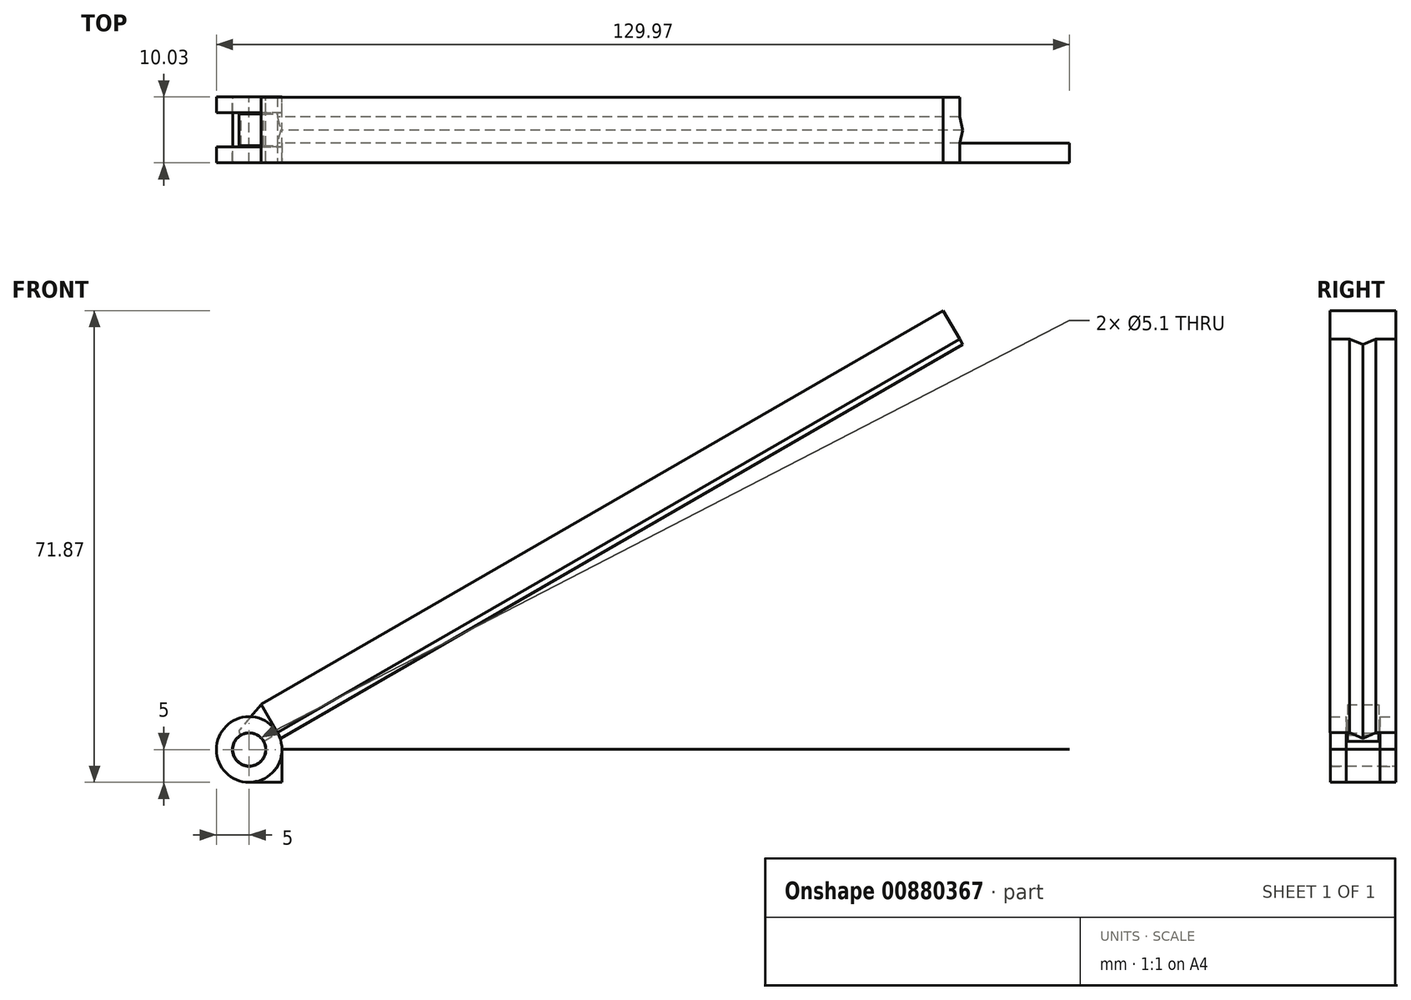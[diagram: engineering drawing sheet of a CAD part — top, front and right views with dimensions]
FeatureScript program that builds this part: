
annotation { "Feature Type Name" : "Feature", "Feature Type Description" : "" }
export const myFeature = defineFeature(function(context is Context, id is Id, definition is map)
    precondition{}
    {
        {
            assignVariable(context, id + "F0", {"name" : "len", "anyValue" : 1.33});
        }
        {
            var Q0;
            Q0=qCreatedBy(makeId("Front.planeOp"),FACE);
            var sketch = newSketch(context, id + "F1", { "sketchPlane" : qUnion([Q0])});
            skPoint(sketch, "E0.middle", {"position": v(0, 0) * mm});
            skLineSegment(sketch, "E1", {"start": v(0, -47.5) * mm, "end": v(0, -45) * mm});
            skLineSegment(sketch, "E2", {"start": v(0, -45) * mm, "end": v(0, 74.97) * mm});
            skLineSegment(sketch, "E3", {"start": v(-5, 74.97) * mm, "end": v(0, 74.97) * mm});
            skLineSegment(sketch, "E4", {"start": v(-5, -45) * mm, "end": v(-5, 74.97) * mm});
            skLineSegment(sketch, "E5", {"start": v(-5, -45) * mm, "end": v(-3.35, -49.75) * mm});
            skPoint(sketch, "E6.visualSharp", {"position": v(-3.26, -50) * mm});
            skCircle(sketch, "E7", {"center": v(0, -50) * mm, "radius": 2.5 * mm});
            skPoint(sketch, "E8.orphan", {"position": v(0, -48.75) * mm});
            skLineSegment(sketch, "E9", {"start": v(-2.5, -50) * mm, "end": v(-3, -50) * mm});
            skArc(sketch, "E10.filletArc", {"start": v(-3.35, -49.75) * mm, "mid": v(-3.22, -49.93) * mm, "end": v(-3, -50) * mm});
            skLineSegment(sketch, "E11", {"start": v(-5, -45) * mm, "end": v(0, -45) * mm});
            skSolve(sketch);
        }
        {
            var Q0;
            Q0=qCreatedBy(makeId("Top.planeOp"),FACE);
            var sketch = newSketch(context, id + "F2", { "sketchPlane" : qUnion([Q0])});
            skPoint(sketch, "E12.middle", {"position": v(-2.56, -0.03) * mm});
            skPoint(sketch, "E13.middle", {"position": v(0, 0) * mm});
            skPoint(sketch, "E14", {"position": v(0.94, -0.03) * mm});
            skLineSegment(sketch, "E15", {"start": v(-5.06, 4.97) * mm, "end": v(-0.06, 4.97) * mm});
            skLineSegment(sketch, "E16", {"start": v(-0.06, 4.97) * mm, "end": v(-0.06, 1.97) * mm});
            skLineSegment(sketch, "E17", {"start": v(-0.06, 1.97) * mm, "end": v(0.94, -0.03) * mm});
            skLineSegment(sketch, "E18", {"start": v(0.94, -0.03) * mm, "end": v(-0.06, -2.03) * mm});
            skLineSegment(sketch, "E19", {"start": v(-0.06, -2.03) * mm, "end": v(-0.06, -5.03) * mm});
            skLineSegment(sketch, "E20", {"start": v(-0.06, -5.03) * mm, "end": v(-5.06, -5.03) * mm});
            skLineSegment(sketch, "E21", {"start": v(-5.06, 4.97) * mm, "end": v(-5.06, -5.03) * mm});
            skLineSegment(sketch, "E22", {"start": v(-2.56, -10.75) * mm, "end": v(-2.56, 12.56) * mm, "construction": true});
            skPoint(sketch, "E22.endSnap0", {"position": v(-2.56, -5.03) * mm});
            skSolve(sketch);
        }
        {
            var Q0;
            Q0=makeQuery(id+"F2.imprint","IMPRINT",FACE,{"disambiguationData":[TD([[makeQuery(id+"F2.imprint","IMPRINT",EDGE,{"derivedFrom":sQuery(id+"F2.wireOp",EDGE,"E15")}),-1.0]])]});
            extrude(context, id + "F3", {"entities" : qUnion([Q0]), "depth" : ((getVariable(context, 'len') * 90) - 45) * mm, "offsetDistance" : 25 * mm, "hasSecondDirection" : true, "secondDirectionOppositeDirection" : true, "secondDirectionDepth" : 45 * mm});
        }
        {
            var Q0;
            {var subQ0=sQuery(id+"F1.wireOp",EDGE,"E7");var subQ1=makeQuery(id+"F1.imprint","INTERSECT",VERTEX,{"derivedFrom":[sQuery(id+"F1.wireOp",EDGE,"y2ifkrbQ-fr0k-EV40-WAJp-tS3gvMkOgowK"),subQ0]});Q0=makeQuery(id+"F1.imprint","IMPRINT",FACE,{"disambiguationData":[TD([[makeQuery(id+"F1.imprint","IMPRINT",EDGE,{"disambiguationData":[TD([[subQ1,1.0]])],"derivedFrom":subQ0}),1.0]])]});}
            extrude(context, id + "F4", {"entities" : qUnion([Q0]), "operationType" : NewBodyOperationType.ADD, "depth" : 5 * mm, "offsetDistance" : 25 * mm, "hasSecondDirection" : true, "secondDirectionOppositeDirection" : true, "secondDirectionDepth" : 5 * mm});
        }
        {
            var Q0;
            {var subQ2=sQuery(id+"F1.wireOp",EDGE,"E1");Q0=makeQuery(id+"F1.imprint","IMPRINT",FACE,{"disambiguationData":[TD([[makeQuery(id+"F1.imprint","IMPRINT",EDGE,{"derivedFrom":subQ2}),1.0]])]});}
            extrude(context, id + "F5", {"entities" : qUnion([Q0]), "depth" : 2.4 * mm, "offsetDistance" : 25 * mm, "hasSecondDirection" : true, "secondDirectionOppositeDirection" : true, "secondDirectionDepth" : 2.4 * mm});
        }
        {
            var Q0;
            Q0=makeQuery(id+"F4.opExtrude","CAP_FACE",FACE,{"disambiguationData":[OSD([sQuery(id+"F1.wireOp",EDGE,"E7")])],"isStart":false});
            var Q1;
            Q1=makeQuery(id+"F4.opExtrude","CAP_FACE",FACE,{"disambiguationData":[OSD([sQuery(id+"F1.wireOp",EDGE,"E7")])],"isStart":true});
            fillet(context, id + "F6", {"entities" : qUnion([Q0, Q1]), "radius" : .25 * mm, "tangentPropagation" : true, "allowEdgeOverflow" : false});
        }
        {
            var Q0;
            Q0=makeQuery(id+"F3.opExtrude","SWEPT_FACE",FACE,{"disambiguationData":[OSD([sQuery(id+"F2.wireOp",EDGE,"ip5yjFWY-FGmT-liJ9-8fW3-jcPs83EoBgNt")])]});
            var Q1;
            Q1=qCreatedBy(makeId("Front.planeOp"),FACE);
            cPlane(context, id + "F7", {"entities" : qUnion([Q0, Q1]), "cplaneType" : CPlaneType.OFFSET, "offset" : 0 * mm, "width" : 150 * mm, "height" : 150 * mm});
        }
        {
            var Q0;
            Q0=qCreatedBy(id+"F7.planeOp",FACE);
            var sketch = newSketch(context, id + "F8", { "sketchPlane" : qUnion([Q0])});
            skPoint(sketch, "E23", {"position": v(0, -50) * mm});
            skCircle(sketch, "E24", {"center": v(0, -50) * mm, "radius": 124.97 * mm, "construction": true});
            skLineSegment(sketch, "E25.right", {"start": v(5, -50) * mm, "end": v(5, -55) * mm});
            skLineSegment(sketch, "E26", {"start": v(5, -50) * mm, "end": v(124.97, -50) * mm});
            skLineSegment(sketch, "E27", {"start": v(124.97, -55) * mm, "end": v(125.37, -55) * mm});
            skLineSegment(sketch, "E28", {"start": v(125.37, -43.8) * mm, "end": v(122.57, -43.8) * mm});
            skLineSegment(sketch, "E29", {"start": v(127.37, -55) * mm, "end": v(125.37, -55) * mm});
            skLineSegment(sketch, "E30", {"start": v(127.37, -37.65) * mm, "end": v(127.37, -55) * mm});
            skLineSegment(sketch, "E31", {"start": v(125.37, -43.8) * mm, "end": v(125.37, -53.5) * mm});
            skLineSegment(sketch, "E32", {"start": v(124.97, -50) * mm, "end": v(125.37, -50) * mm});
            skLineSegment(sketch, "E33", {"start": v(5, -50) * mm, "end": v(5, -32.35) * mm, "construction": true});
            skLineSegment(sketch, "E34", {"start": v(122.57, -43.8) * mm, "end": v(126.7, -37.45) * mm});
            skCircle(sketch, "E35", {"center": v(0, -50) * mm, "radius": 5 * mm});
            skCircle(sketch, "E36", {"center": v(0, -50) * mm, "radius": 3 * mm});
            skLineSegment(sketch, "E37", {"start": v(-3, -50) * mm, "end": v(-5, -50) * mm});
            skLineSegment(sketch, "E38", {"start": v(0, -47) * mm, "end": v(0, -45) * mm});
            skLineSegment(sketch, "E39", {"start": v(124.97, -55) * mm, "end": v(0, -55) * mm});
            skPoint(sketch, "E40.visualSharp", {"position": v(127.37, -36.4) * mm});
            skArc(sketch, "E40.filletArc", {"start": v(127.37, -37.65) * mm, "mid": v(127.1, -37.3) * mm, "end": v(126.7, -37.45) * mm});
            skLineSegment(sketch, "E41", {"start": v(125.37, -53.5) * mm, "end": v(117.37, -53.5) * mm});
            skLineSegment(sketch, "E42", {"start": v(117.37, -53.1) * mm, "end": v(117.37, -53.5) * mm});
            skLineSegment(sketch, "E43", {"start": v(117.37, -53.1) * mm, "end": v(124.93, -53.1) * mm});
            skLineSegment(sketch, "E44", {"start": v(124.93, -53.1) * mm, "end": v(124.97, -50) * mm});
            skLineSegment(sketch, "E45", {"start": v(117.37, -53.5) * mm, "end": v(117.37, -55) * mm});
            skSolve(sketch);
        }
        {
            var Q0;
            Q0=qCreatedBy(makeId("Right.planeOp"),FACE);
            var sketch = newSketch(context, id + "F9", { "sketchPlane" : qUnion([Q0])});
            skLineSegment(sketch, "E46", {"start": v(0, -59.14) * mm, "end": v(0, -40.5) * mm, "construction": true});
            skPoint(sketch, "E47", {"position": v(-5, -50.02) * mm});
            skLineSegment(sketch, "E48", {"start": v(-5, -45.02) * mm, "end": v(-2.59, -45.02) * mm});
            skLineSegment(sketch, "E49", {"start": v(-2.59, -50.02) * mm, "end": v(-5, -50.02) * mm, "construction": true});
            skLineSegment(sketch, "E50.MirrorCS", {"start": v(5, -45.02) * mm, "end": v(2.59, -45.02) * mm});
            skLineSegment(sketch, "E51.MirrorCS", {"start": v(5, -50.02) * mm, "end": v(5, -45.02) * mm, "construction": true});
            skLineSegment(sketch, "E52.MirrorCS", {"start": v(2.59, -50.02) * mm, "end": v(5, -50.02) * mm, "construction": true});
            skLineSegment(sketch, "E53", {"start": v(6.96, -50.02) * mm, "end": v(-6.61, -50.02) * mm, "construction": true});
            skLineSegment(sketch, "E54", {"start": v(-5.97, -50.02) * mm, "end": v(-5.97, -47.47) * mm, "construction": true});
            skLineSegment(sketch, "E55", {"start": v(-5, -45.02) * mm, "end": v(-5, -47.47) * mm});
            skLineSegment(sketch, "E56", {"start": v(-5, -47.47) * mm, "end": v(-2.59, -47.47) * mm});
            skLineSegment(sketch, "E57", {"start": v(-2.59, -47.47) * mm, "end": v(-2.59, -45.02) * mm});
            skLineSegment(sketch, "E58.MirrorCS", {"start": v(5, -45.02) * mm, "end": v(5, -47.47) * mm});
            skLineSegment(sketch, "E59.MirrorCS", {"start": v(2.59, -47.47) * mm, "end": v(2.59, -45.02) * mm});
            skLineSegment(sketch, "E60.MirrorCS", {"start": v(5, -47.47) * mm, "end": v(2.59, -47.47) * mm});
            skSolve(sketch);
        }
        {
            var Q0;
            Q0=qSketchRegion(id+"F9",true);
            var Q1;
            Q1=sQuery(id+"F9.wireOp",EDGE,"E53");
            revolve(context, id + "F10", {"surfaceOperationType" : NewSurfaceOperationType.NEW, "entities" : qUnion([Q0]), "axis" : qUnion([Q1]), "revolveType" : RevolveType.FULL});
        }
        {
            var Q0;
            {var subQ4=sQuery(id+"F8.wireOp",EDGE,"E25.right");Q0=makeQuery(id+"F8.imprint","IMPRINT",FACE,{"disambiguationData":[TD([[makeQuery(id+"F8.imprint","IMPRINT",EDGE,{"derivedFrom":subQ4}),-1.0]])]});}
            extrude(context, id + "F11", {"entities" : qUnion([Q0]), "depth" : 5 * mm, "offsetDistance" : 25 * mm, "hasSecondDirection" : true, "secondDirectionOppositeDirection" : true, "secondDirectionDepth" : 5 * mm});
        }
        {
            var Q0;
            Q0=makeQuery(id+"F11.opExtrude","SWEPT_FACE",FACE,{"disambiguationData":[OSD([sQuery(id+"F8.wireOp",EDGE,"E25.right")])]});
            var Q1;
            Q1=qBodyType(qCreatedBy(id+"F13",EDGE),BodyType.WIRE);
            cPlane(context, id + "F12", {"entities" : qUnion([Q0, Q1]), "cplaneType" : CPlaneType.OFFSET, "offset" : 0 * mm, "width" : 150 * mm, "height" : 150 * mm});
        }
        {
            var Q0;
            Q0=qCreatedBy(id+"F12.planeOp",FACE);
            var sketch = newSketch(context, id + "F13", { "sketchPlane" : qUnion([Q0])});
            skPoint(sketch, "E61", {"position": v(0, -52.5) * mm});
            skLineSegment(sketch, "E62", {"start": v(-7.37, -52.5) * mm, "end": v(6.54, -52.5) * mm, "construction": true});
            skPoint(sketch, "E63.middle", {"position": v(0, -50) * mm});
            skLineSegment(sketch, "E64", {"start": v(0, -55) * mm, "end": v(0, -48.4) * mm, "construction": true});
            skPoint(sketch, "E65", {"position": v(-5, -50) * mm});
            skPoint(sketch, "E66", {"position": v(-2, -50) * mm});
            skPoint(sketch, "E67", {"position": v(2, -50) * mm});
            skPoint(sketch, "E68", {"position": v(5, -50) * mm});
            skLineSegment(sketch, "E69", {"start": v(-5, -50) * mm, "end": v(-5, -50) * mm});
            skLineSegment(sketch, "E70", {"start": v(-5, -50) * mm, "end": v(-2, -50) * mm});
            skLineSegment(sketch, "E71", {"start": v(2, -50) * mm, "end": v(5, -50) * mm});
            skLineSegment(sketch, "E72", {"start": v(5, -50) * mm, "end": v(5, -50) * mm});
            skLineSegment(sketch, "E73", {"start": v(5, -50) * mm, "end": v(2, -50) * mm});
            skLineSegment(sketch, "E74", {"start": v(3.05, -50) * mm, "end": v(3.05, -52) * mm, "construction": true});
            skPoint(sketch, "E75", {"position": v(0, -52) * mm});
            skLineSegment(sketch, "E76", {"start": v(2, -50) * mm, "end": v(0, -52) * mm});
            skLineSegment(sketch, "E77", {"start": v(-2, -50) * mm, "end": v(0, -52) * mm});
            skLineSegment(sketch, "E78", {"start": v(5, -50) * mm, "end": v(5, -55) * mm});
            skLineSegment(sketch, "E79", {"start": v(5, -55) * mm, "end": v(-5, -55) * mm});
            skLineSegment(sketch, "E80", {"start": v(-5, -55) * mm, "end": v(-5, -50) * mm});
            skLineSegment(sketch, "E81.trimOffspring", {"start": v(-2, -50) * mm, "end": v(-5, -50) * mm});
            skSolve(sketch);
        }
        {
            var Q0;
            {var subQ1=sQuery(id+"F13.wireOp",EDGE,"E70");Q0=makeQuery(id+"F13.imprint","IMPRINT",FACE,{"disambiguationData":[TD([[makeQuery(id+"F13.imprint","IMPRINT",EDGE,{"derivedFrom":subQ1}),-1.0]])]});}
            extrude(context, id + "F14", {"entities" : qUnion([Q0]), "depth" : (getVariable(context, 'len') * 90) * mm, "offsetDistance" : 25 * mm});
        }
        {
            var Q0;
            {var subQ1=sQuery(id+"F8.wireOp",EDGE,"E32");Q0=makeQuery(id+"F8.imprint","IMPRINT",FACE,{"disambiguationData":[TD([[makeQuery(id+"F8.imprint","IMPRINT",EDGE,{"derivedFrom":subQ1}),-1.0]])]});}
            extrude(context, id + "F15", {"entities" : qUnion([Q0]), "operationType" : NewBodyOperationType.REMOVE, "depth" : 5 * mm, "offsetDistance" : 25 * mm, "hasSecondDirection" : true, "secondDirectionOppositeDirection" : true, "secondDirectionDepth" : 5 * mm});
        }
        {
            var Q0;
            Q0=makeQuery(id+"F3.opExtrude","SWEPT_BODY",BODY,{"disambiguationData":[OSD([sQuery(id+"F2.wireOp",EDGE,"E15"),sQuery(id+"F2.wireOp",EDGE,"E16"),sQuery(id+"F2.wireOp",EDGE,"E17"),sQuery(id+"F2.wireOp",EDGE,"E18"),sQuery(id+"F2.wireOp",EDGE,"E19"),sQuery(id+"F2.wireOp",EDGE,"E20"),sQuery(id+"F2.wireOp",EDGE,"E21")])]});
            var Q1;
            Q1=makeQuery(id+"F5.opExtrude","SWEPT_BODY",BODY,{"disambiguationData":[OSD([sQuery(id+"F1.wireOp",EDGE,"E1"),sQuery(id+"F1.wireOp",EDGE,"E5"),sQuery(id+"F1.wireOp",EDGE,"E7"),sQuery(id+"F1.wireOp",EDGE,"E9"),sQuery(id+"F1.wireOp",EDGE,"E10.filletArc"),sQuery(id+"F1.wireOp",EDGE,"E11")])]});
            var Q2;
            Q2=makeQuery(id+"F4.opExtrude","SWEPT_BODY",BODY,{"disambiguationData":[OSD([sQuery(id+"F1.wireOp",EDGE,"E7")])]});
            var Q3;
            Q3=sQuery(id+"F9.wireOp",EDGE,"E53");
            transform(context, id + "F16", {"entities" : qUnion([Q0, Q1, Q2]), "transformType" : TransformType.ROTATION, "transformAxis" : qUnion([Q3]), "angle" : 60 * degree, "oppositeDirection" : true, "makeCopy" : false});
        }
    });
